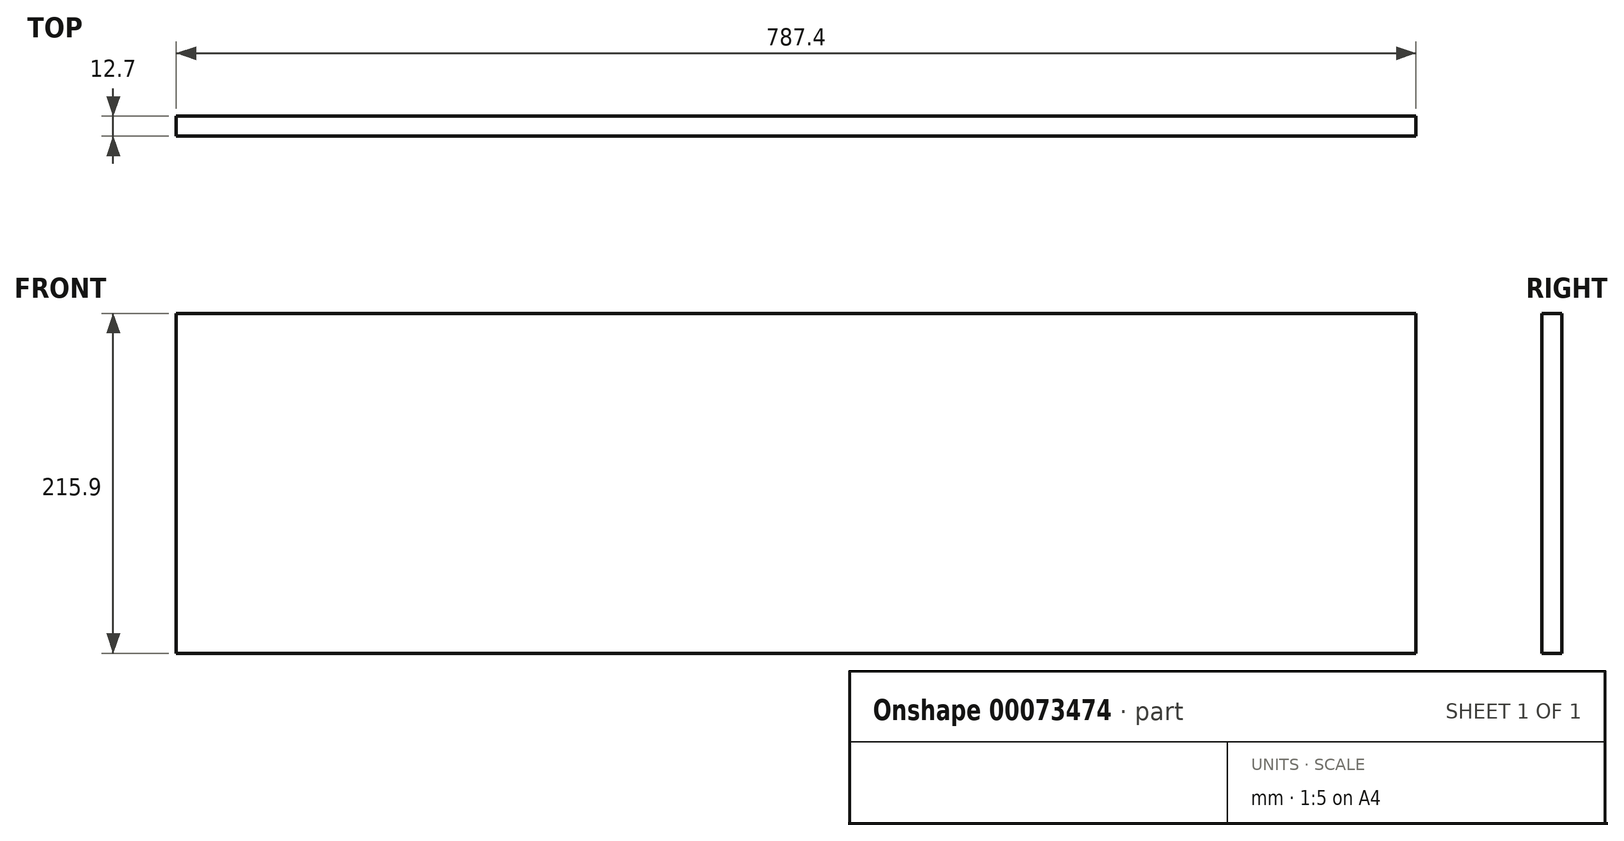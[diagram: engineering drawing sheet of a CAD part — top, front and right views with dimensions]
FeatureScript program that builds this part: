
annotation { "Feature Type Name" : "Feature", "Feature Type Description" : "" }
export const myFeature = defineFeature(function(context is Context, id is Id, definition is map)
    precondition{}
    {
        {
            var Q0;
            Q0=qCreatedBy(makeId("Front.planeOp"),FACE);
            var sketch = newSketch(context, id + "F0", { "sketchPlane" : qUnion([Q0])});
            skLineSegment(sketch, "E0.bottom", {"start": v(-393.24, -227.43) * mm, "end": v(394.16, -227.43) * mm});
            skLineSegment(sketch, "E0.top", {"start": v(-393.24, -11.53) * mm, "end": v(394.16, -11.53) * mm});
            skLineSegment(sketch, "E0.left", {"start": v(-393.24, -227.43) * mm, "end": v(-393.24, -11.53) * mm});
            skLineSegment(sketch, "E0.right", {"start": v(394.16, -227.43) * mm, "end": v(394.16, -11.53) * mm});
            skSolve(sketch);
        }
        {
            var Q0;
            Q0=makeQuery(id+"F0.imprint","IMPRINT",FACE,{"disambiguationData":[TD([[makeQuery(id+"F0.imprint","IMPRINT",EDGE,{"derivedFrom":sQuery(id+"F0.wireOp",EDGE,"E0.bottom")}),1.0]])]});
            extrude(context, id + "F1", {"entities" : qUnion([Q0]), "depth" : 12.7 * mm});
        }
    });
